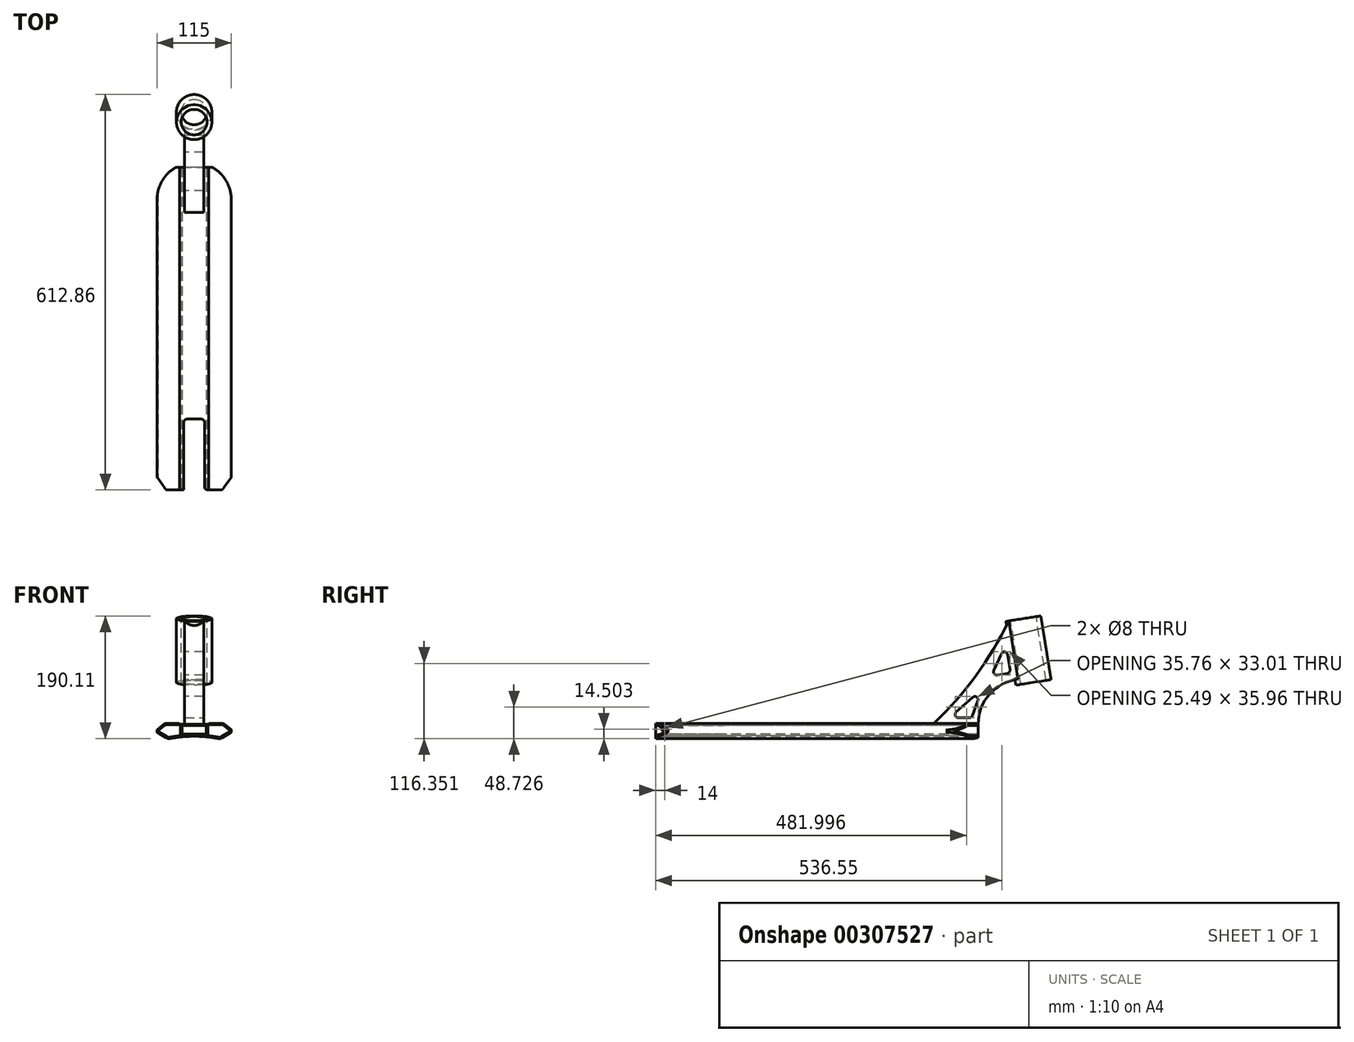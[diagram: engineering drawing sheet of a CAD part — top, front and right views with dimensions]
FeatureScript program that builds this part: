
annotation { "Feature Type Name" : "Feature", "Feature Type Description" : "" }
export const myFeature = defineFeature(function(context is Context, id is Id, definition is map)
    precondition{}
    {
        {
            var Q0;
            Q0=qCreatedBy(makeId("Front.planeOp"),FACE);
            var sketch = newSketch(context, id + "F0", { "sketchPlane" : qUnion([Q0])});
            skLineSegment(sketch, "E0", {"start": v(0, 0) * mm, "end": v(0, 36.76) * mm});
            skLineSegment(sketch, "E1", {"start": v(0, 0) * mm, "end": v(22.5, 0) * mm});
            skLineSegment(sketch, "E2", {"start": v(22.5, 0) * mm, "end": v(22.5, 1.3) * mm});
            skLineSegment(sketch, "E3", {"start": v(22.5, 1.3) * mm, "end": v(45.58, 1.3) * mm});
            skLineSegment(sketch, "E4", {"start": v(45.58, 1.3) * mm, "end": v(57.5, -8.7) * mm});
            skLineSegment(sketch, "E5", {"start": v(57.5, -8.7) * mm, "end": v(57.5, -12.7) * mm});
            skLineSegment(sketch, "E6", {"start": v(57.5, -12.7) * mm, "end": v(40.18, -22.7) * mm});
            skLineSegment(sketch, "E7.MirrorCS", {"start": v(0, 0) * mm, "end": v(-22.5, 0) * mm});
            skLineSegment(sketch, "E8.MirrorCS", {"start": v(-22.5, 1.3) * mm, "end": v(-45.58, 1.3) * mm});
            skLineSegment(sketch, "E9.MirrorCS", {"start": v(-22.5, 0) * mm, "end": v(-22.5, 1.3) * mm});
            skLineSegment(sketch, "E10.MirrorCS", {"start": v(-45.58, 1.3) * mm, "end": v(-57.5, -8.7) * mm});
            skLineSegment(sketch, "E11.MirrorCS", {"start": v(-57.5, -8.7) * mm, "end": v(-57.5, -12.7) * mm});
            skLineSegment(sketch, "E12.MirrorCS", {"start": v(-57.5, -12.7) * mm, "end": v(-40.18, -22.7) * mm});
            skArc(sketch, "E13", {"start": v(40.18, -22.7) * mm, "mid": v(0, -18.62) * mm, "end": v(-40.18, -22.7) * mm});
            skSolve(sketch);
        }
        {
            var Q0;
            Q0 = qSketchRegion(id + "F0", true);
            extrude(context, id + "F1", {"entities" : qUnion([Q0]), "endBound" : BoundingType.SYMMETRIC, "depth" : 500 * mm});
        }
        {
            var Q0;
            Q0=qCreatedBy(makeId("Front.planeOp"),FACE);
            var sketch = newSketch(context, id + "F2", { "sketchPlane" : qUnion([Q0])});
            skLineSegment(sketch, "E14.bottom", {"start": v(-19, -2) * mm, "end": v(19, -2) * mm});
            skLineSegment(sketch, "E14.top", {"start": v(-19, -15) * mm, "end": v(19, -15) * mm});
            skLineSegment(sketch, "E14.left", {"start": v(-19, -2) * mm, "end": v(-19, -15) * mm});
            skLineSegment(sketch, "E14.right", {"start": v(19, -2) * mm, "end": v(19, -15) * mm});
            skSolve(sketch);
        }
        {
            var Q0;
            Q0 = qSketchRegion(id + "F2", true);
            extrude(context, id + "F3", {"entities" : qUnion([Q0]), "operationType" : NewBodyOperationType.REMOVE, "endBound" : BoundingType.SYMMETRIC, "oppositeDirection" : true, "depth" : 500 * mm});
        }
        {
            var Q0;
            Q0=makeQuery(id+"F1.opExtrude","SWEPT_EDGE",EDGE,{"disambiguationData":[OSD([sQuery(id+"F0.wireOp",EDGE,"E2"),sQuery(id+"F0.wireOp",EDGE,"E3")])]});
            var Q1;
            Q1=makeQuery(id+"F1.opExtrude","SWEPT_EDGE",EDGE,{"disambiguationData":[OSD([sQuery(id+"F0.wireOp",EDGE,"E8.MirrorCS"),sQuery(id+"F0.wireOp",EDGE,"E9.MirrorCS")])]});
            fillet(context, id + "F4", {"entities" : qUnion([Q0, Q1]), "radius" : 2 * mm, "tangentPropagation" : true, "allowEdgeOverflow" : false});
        }
        {
            var Q0;
            Q0=makeQuery(id+"F1.opExtrude","SWEPT_EDGE",EDGE,{"disambiguationData":[OSD([sQuery(id+"F0.wireOp",EDGE,"E3"),sQuery(id+"F0.wireOp",EDGE,"E4")])]});
            var Q1;
            Q1=makeQuery(id+"F1.opExtrude","SWEPT_EDGE",EDGE,{"disambiguationData":[OSD([sQuery(id+"F0.wireOp",EDGE,"E8.MirrorCS"),sQuery(id+"F0.wireOp",EDGE,"E10.MirrorCS")])]});
            var Q2;
            Q2=makeQuery(id+"F1.opExtrude","SWEPT_EDGE",EDGE,{"disambiguationData":[OSD([sQuery(id+"F0.wireOp",EDGE,"E6"),sQuery(id+"F0.wireOp",EDGE,"E13")])]});
            var Q3;
            Q3=makeQuery(id+"F1.opExtrude","SWEPT_EDGE",EDGE,{"disambiguationData":[OSD([sQuery(id+"F0.wireOp",EDGE,"E12.MirrorCS"),sQuery(id+"F0.wireOp",EDGE,"E13")])]});
            fillet(context, id + "F5", {"entities" : qUnion([Q0, Q1, Q2, Q3]), "radius" : 9 * mm, "tangentPropagation" : true, "allowEdgeOverflow" : false});
        }
        {
            var Q0;
            Q0=makeQuery(id+"F1.opExtrude","SWEPT_EDGE",EDGE,{"disambiguationData":[OSD([sQuery(id+"F0.wireOp",EDGE,"E4"),sQuery(id+"F0.wireOp",EDGE,"E5")])]});
            var Q1;
            Q1=makeQuery(id+"F1.opExtrude","SWEPT_EDGE",EDGE,{"disambiguationData":[OSD([sQuery(id+"F0.wireOp",EDGE,"E5"),sQuery(id+"F0.wireOp",EDGE,"E6")])]});
            var Q2;
            Q2=makeQuery(id+"F1.opExtrude","SWEPT_EDGE",EDGE,{"disambiguationData":[OSD([sQuery(id+"F0.wireOp",EDGE,"E10.MirrorCS"),sQuery(id+"F0.wireOp",EDGE,"E11.MirrorCS")])]});
            var Q3;
            Q3=makeQuery(id+"F1.opExtrude","SWEPT_EDGE",EDGE,{"disambiguationData":[OSD([sQuery(id+"F0.wireOp",EDGE,"E11.MirrorCS"),sQuery(id+"F0.wireOp",EDGE,"E12.MirrorCS")])]});
            fillet(context, id + "F6", {"entities" : qUnion([Q0, Q1, Q2, Q3]), "radius" : 1 * mm, "tangentPropagation" : true, "allowEdgeOverflow" : false});
        }
        {
            var Q0;
            Q0=makeQuery(id+"F1.opExtrude","CAP_FACE",FACE,{"disambiguationData":[OSD([sQuery(id+"F0.wireOp",EDGE,"E1"),sQuery(id+"F0.wireOp",EDGE,"E2"),sQuery(id+"F0.wireOp",EDGE,"E3"),sQuery(id+"F0.wireOp",EDGE,"E4"),sQuery(id+"F0.wireOp",EDGE,"E5"),sQuery(id+"F0.wireOp",EDGE,"E6"),sQuery(id+"F0.wireOp",EDGE,"E7.MirrorCS"),sQuery(id+"F0.wireOp",EDGE,"E8.MirrorCS"),sQuery(id+"F0.wireOp",EDGE,"E9.MirrorCS"),sQuery(id+"F0.wireOp",EDGE,"E10.MirrorCS"),sQuery(id+"F0.wireOp",EDGE,"E11.MirrorCS"),sQuery(id+"F0.wireOp",EDGE,"E12.MirrorCS"),sQuery(id+"F0.wireOp",EDGE,"E13")])],"isStart":false});
            var sketch = newSketch(context, id + "F7", { "sketchPlane" : qUnion([Q0])});
            skArc(sketch, "E15.0", {"start": v(37.3, -20.1) * mm, "mid": v(0, -16.62) * mm, "end": v(-37.3, -20.1) * mm});
            skArc(sketch, "E15.1", {"start": v(-42.1, -19.28) * mm, "mid": v(-39.78, -20.12) * mm, "end": v(-37.3, -20.1) * mm});
            skLineSegment(sketch, "E15.2", {"start": v(-24.37, -0.7) * mm, "end": v(-42.3, -0.7) * mm});
            skArc(sketch, "E15.3", {"start": v(-42.3, -0.7) * mm, "mid": v(-44.7, -1.12) * mm, "end": v(-46.8, -2.34) * mm});
            skLineSegment(sketch, "E15.4", {"start": v(-46.8, -2.34) * mm, "end": v(-55.76, -9.85) * mm});
            skLineSegment(sketch, "E15.5", {"start": v(-55.61, -11.48) * mm, "end": v(-42.1, -19.28) * mm});
            skPoint(sketch, "E16.visualSharp", {"position": v(-56.85, -10.77) * mm});
            skArc(sketch, "E16.filletArc", {"start": v(-55.76, -9.85) * mm, "mid": v(-56.1, -10.7) * mm, "end": v(-55.61, -11.48) * mm});
            skArc(sketch, "E17", {"start": v(-22.5, -2) * mm, "mid": v(-23.23, -1.06) * mm, "end": v(-24.37, -0.7) * mm});
            skLineSegment(sketch, "E18", {"start": v(-22.5, -2) * mm, "end": v(-21, -2) * mm});
            skLineSegment(sketch, "E19", {"start": v(-21, -2) * mm, "end": v(-21, -17.72) * mm});
            skLineSegment(sketch, "E20.MirrorCS", {"start": v(21, -2) * mm, "end": v(21, -17.72) * mm});
            skLineSegment(sketch, "E21.MirrorCS", {"start": v(22.5, -2) * mm, "end": v(21, -2) * mm});
            skArc(sketch, "E22.MirrorCS", {"start": v(22.5, -2) * mm, "mid": v(23.23, -1.06) * mm, "end": v(24.37, -0.7) * mm});
            skLineSegment(sketch, "E23.MirrorCS", {"start": v(24.37, -0.7) * mm, "end": v(42.3, -0.7) * mm});
            skArc(sketch, "E24.MirrorCS", {"start": v(42.3, -0.7) * mm, "mid": v(44.7, -1.12) * mm, "end": v(46.8, -2.34) * mm});
            skLineSegment(sketch, "E25.MirrorCS", {"start": v(46.8, -2.34) * mm, "end": v(55.76, -9.85) * mm});
            skArc(sketch, "E26.MirrorCS", {"start": v(55.76, -9.85) * mm, "mid": v(56.1, -10.7) * mm, "end": v(55.61, -11.48) * mm});
            skLineSegment(sketch, "E27.MirrorCS", {"start": v(55.61, -11.48) * mm, "end": v(42.1, -19.28) * mm});
            skArc(sketch, "E28.MirrorCS", {"start": v(42.1, -19.28) * mm, "mid": v(39.78, -20.12) * mm, "end": v(37.3, -20.1) * mm});
            skArc(sketch, "E29.MirrorCS", {"start": v(-37.3, -20.1) * mm, "mid": v(0, -16.62) * mm, "end": v(37.3, -20.1) * mm});
            skSolve(sketch);
        }
        {
            var Q0;
            {var subQ0=sQuery(id+"F7.wireOp",EDGE,"E15.1");Q0=makeQuery(id+"F7.imprint","IMPRINT",FACE,{"disambiguationData":[TD([[makeQuery(id+"F7.imprint","IMPRINT",EDGE,{"derivedFrom":subQ0}),1.0]])]});}
            var Q1;
            {var subQ0=sQuery(id+"F7.wireOp",EDGE,"E20.MirrorCS");Q1=makeQuery(id+"F7.imprint","IMPRINT",FACE,{"disambiguationData":[TD([[makeQuery(id+"F7.imprint","IMPRINT",EDGE,{"derivedFrom":subQ0}),1.0]])]});}
            extrude(context, id + "F8", {"entities" : qUnion([Q0, Q1]), "operationType" : NewBodyOperationType.REMOVE, "endBound" : BoundingType.THROUGH_ALL, "oppositeDirection" : true, "depth" : 25 * mm});
        }
        {
            var Q0;
            Q0=qCreatedBy(makeId("Top.planeOp"),FACE);
            var sketch = newSketch(context, id + "F9", { "sketchPlane" : qUnion([Q0])});
            skArc(sketch, "E30", {"start": v(57.5, 200) * mm, "mid": v(0, 257.5) * mm, "end": v(-57.5, 200) * mm});
            skLineSegment(sketch, "E31", {"start": v(-57.5, 200) * mm, "end": v(-57.5, 280) * mm});
            skLineSegment(sketch, "E32", {"start": v(-57.5, 280) * mm, "end": v(57.5, 280) * mm});
            skLineSegment(sketch, "E33", {"start": v(57.5, 280) * mm, "end": v(57.5, 200) * mm});
            skSolve(sketch);
        }
        {
            var Q0;
            Q0=makeQuery(id+"F9.imprint","IMPRINT",FACE,{"disambiguationData":[TD([[makeQuery(id+"F9.imprint","IMPRINT",EDGE,{"derivedFrom":sQuery(id+"F9.wireOp",EDGE,"E30")}),-1.0]])]});
            extrude(context, id + "F10", {"entities" : qUnion([Q0]), "operationType" : NewBodyOperationType.REMOVE, "endBound" : BoundingType.THROUGH_ALL, "depth" : 25 * mm, "hasSecondDirection" : true, "secondDirectionBound" : SecondDirectionBoundingType.THROUGH_ALL, "secondDirectionOppositeDirection" : true, "secondDirectionDepth" : 25 * mm});
        }
        {
            var Q0;
            Q0=qCreatedBy(makeId("Top.planeOp"),FACE);
            var sketch = newSketch(context, id + "F11", { "sketchPlane" : qUnion([Q0])});
            skLineSegment(sketch, "E34", {"start": v(-68, -216) * mm, "end": v(-43.3, -250) * mm});
            skLineSegment(sketch, "E35", {"start": v(-43.3, -250) * mm, "end": v(-16, -250) * mm});
            skLineSegment(sketch, "E36", {"start": v(-16, -250) * mm, "end": v(-16, -140) * mm});
            skLineSegment(sketch, "E37", {"start": v(-16, -140) * mm, "end": v(16, -140) * mm});
            skLineSegment(sketch, "E38", {"start": v(16, -140) * mm, "end": v(16, -250) * mm});
            skLineSegment(sketch, "E39", {"start": v(16, -250) * mm, "end": v(43.3, -250) * mm});
            skLineSegment(sketch, "E40", {"start": v(43.3, -250) * mm, "end": v(68, -216) * mm});
            skLineSegment(sketch, "E41", {"start": v(68, -216) * mm, "end": v(68, -346) * mm});
            skLineSegment(sketch, "E42", {"start": v(68, -346) * mm, "end": v(-68, -346) * mm});
            skLineSegment(sketch, "E43", {"start": v(-68, -346) * mm, "end": v(-68, -216) * mm});
            skSolve(sketch);
        }
        {
            var Q0;
            Q0=makeQuery(id+"F11.imprint","IMPRINT",FACE,{"disambiguationData":[TD([[makeQuery(id+"F11.imprint","IMPRINT",EDGE,{"derivedFrom":sQuery(id+"F11.wireOp",EDGE,"E34")}),-1.0]])]});
            extrude(context, id + "F12", {"entities" : qUnion([Q0]), "operationType" : NewBodyOperationType.REMOVE, "endBound" : BoundingType.THROUGH_ALL, "oppositeDirection" : true, "depth" : 25 * mm, "hasSecondDirection" : true, "secondDirectionBound" : SecondDirectionBoundingType.THROUGH_ALL, "secondDirectionOppositeDirection" : false, "secondDirectionDepth" : 25 * mm});
        }
        {
            var Q0;
            {var subQ2=sQuery(id+"F11.wireOp",EDGE,"E36");Q0=makeQuery(id+"F12.boolean.opBoolean","COPY",EDGE,{"disambiguationData":[TD([makeQuery(id+"F3.boolean.opBoolean","COPY",FACE,{"derivedFrom":makeQuery(id+"F3.opExtrude","SWEPT_FACE",FACE,{"disambiguationData":[OSD([sQuery(id+"F2.wireOp",EDGE,"E14.bottom")])]})})])],"derivedFrom":makeQuery(id+"F12.opExtrude","SWEPT_EDGE",EDGE,{"disambiguationData":[OSD([sQuery(id+"F11.wireOp",EDGE,"E35"),subQ2])]})});}
            var Q1;
            {var subQ0=sQuery(id+"F0.wireOp",EDGE,"E13");var subQ1=sQuery(id+"F11.wireOp",EDGE,"E36");Q1=makeQuery(id+"F12.boolean.opBoolean","COPY",EDGE,{"disambiguationData":[TD([makeQuery(id+"F1.opExtrude","SWEPT_FACE",FACE,{"disambiguationData":[OSD([subQ0])]})])],"derivedFrom":makeQuery(id+"F12.opExtrude","SWEPT_EDGE",EDGE,{"disambiguationData":[OSD([sQuery(id+"F11.wireOp",EDGE,"E35"),subQ1])]})});}
            var Q2;
            {var subQ0=sQuery(id+"F11.wireOp",EDGE,"E36");var subQ1=sQuery(id+"F11.wireOp",EDGE,"E37");Q2=makeQuery(id+"F12.boolean.opBoolean","COPY",EDGE,{"disambiguationData":[TD([makeQuery(id+"F3.boolean.opBoolean","COPY",FACE,{"derivedFrom":makeQuery(id+"F3.opExtrude","SWEPT_FACE",FACE,{"disambiguationData":[OSD([sQuery(id+"F2.wireOp",EDGE,"E14.bottom")])]})})])],"derivedFrom":makeQuery(id+"F12.opExtrude","SWEPT_EDGE",EDGE,{"disambiguationData":[OSD([subQ0,subQ1])]})});}
            var Q3;
            {var subQ0=sQuery(id+"F11.wireOp",EDGE,"E37");var subQ1=sQuery(id+"F11.wireOp",EDGE,"E36");Q3=makeQuery(id+"F12.boolean.opBoolean","COPY",EDGE,{"disambiguationData":[TD([makeQuery(id+"F1.opExtrude","SWEPT_FACE",FACE,{"disambiguationData":[OSD([sQuery(id+"F0.wireOp",EDGE,"E13")])]})])],"derivedFrom":makeQuery(id+"F12.opExtrude","SWEPT_EDGE",EDGE,{"disambiguationData":[OSD([subQ1,subQ0])]})});}
            var Q4;
            {var subQ0=sQuery(id+"F11.wireOp",EDGE,"E38");var subQ1=sQuery(id+"F11.wireOp",EDGE,"E37");Q4=makeQuery(id+"F12.boolean.opBoolean","COPY",EDGE,{"disambiguationData":[TD([makeQuery(id+"F3.boolean.opBoolean","COPY",FACE,{"derivedFrom":makeQuery(id+"F3.opExtrude","SWEPT_FACE",FACE,{"disambiguationData":[OSD([sQuery(id+"F2.wireOp",EDGE,"E14.bottom")])]})})])],"derivedFrom":makeQuery(id+"F12.opExtrude","SWEPT_EDGE",EDGE,{"disambiguationData":[OSD([subQ1,subQ0])]})});}
            var Q5;
            {var subQ0=sQuery(id+"F11.wireOp",EDGE,"E37");var subQ1=sQuery(id+"F11.wireOp",EDGE,"E38");Q5=makeQuery(id+"F12.boolean.opBoolean","COPY",EDGE,{"disambiguationData":[TD([makeQuery(id+"F1.opExtrude","SWEPT_FACE",FACE,{"disambiguationData":[OSD([sQuery(id+"F0.wireOp",EDGE,"E13")])]})])],"derivedFrom":makeQuery(id+"F12.opExtrude","SWEPT_EDGE",EDGE,{"disambiguationData":[OSD([subQ0,subQ1])]})});}
            var Q6;
            {var subQ2=sQuery(id+"F11.wireOp",EDGE,"E38");Q6=makeQuery(id+"F12.boolean.opBoolean","COPY",EDGE,{"disambiguationData":[TD([makeQuery(id+"F3.boolean.opBoolean","COPY",FACE,{"derivedFrom":makeQuery(id+"F3.opExtrude","SWEPT_FACE",FACE,{"disambiguationData":[OSD([sQuery(id+"F2.wireOp",EDGE,"E14.bottom")])]})})])],"derivedFrom":makeQuery(id+"F12.opExtrude","SWEPT_EDGE",EDGE,{"disambiguationData":[OSD([subQ2,sQuery(id+"F11.wireOp",EDGE,"E39")])]})});}
            var Q7;
            {var subQ0=sQuery(id+"F0.wireOp",EDGE,"E13");var subQ1=sQuery(id+"F11.wireOp",EDGE,"E38");Q7=makeQuery(id+"F12.boolean.opBoolean","COPY",EDGE,{"disambiguationData":[TD([makeQuery(id+"F1.opExtrude","SWEPT_FACE",FACE,{"disambiguationData":[OSD([subQ0])]})])],"derivedFrom":makeQuery(id+"F12.opExtrude","SWEPT_EDGE",EDGE,{"disambiguationData":[OSD([subQ1,sQuery(id+"F11.wireOp",EDGE,"E39")])]})});}
            fillet(context, id + "F13", {"entities" : qUnion([Q0, Q1, Q2, Q3, Q4, Q5, Q6, Q7]), "radius" : 5 * mm, "tangentPropagation" : true, "allowEdgeOverflow" : false});
        }
        {
            var Q0;
            Q0=qCreatedBy(makeId("Right.planeOp"),FACE);
            var sketch = newSketch(context, id + "F14", { "sketchPlane" : qUnion([Q0])});
            skLineSegment(sketch, "E44", {"start": v(250, 0) * mm, "end": v(180, 0) * mm});
            skArc(sketch, "E45", {"start": v(311.71, 69.5) * mm, "mid": v(267.66, 46.48) * mm, "end": v(250, 0) * mm});
            skArc(sketch, "E46", {"start": v(180, 0) * mm, "mid": v(245.97, 74.66) * mm, "end": v(297.38, 160) * mm});
            skLineSegment(sketch, "E47", {"start": v(297.38, 160) * mm, "end": v(342.82, 167.2) * mm});
            skLineSegment(sketch, "E48", {"start": v(342.82, 167.2) * mm, "end": v(358.46, 68.43) * mm});
            skLineSegment(sketch, "E49", {"start": v(358.46, 68.43) * mm, "end": v(313.03, 61.23) * mm});
            skLineSegment(sketch, "E50", {"start": v(311.71, 69.5) * mm, "end": v(313.03, 61.23) * mm});
            skSolve(sketch);
        }
        {
            var Q0;
            Q0 = qSketchRegion(id + "F14", true);
            extrude(context, id + "F15", {"entities" : qUnion([Q0]), "operationType" : NewBodyOperationType.ADD, "endBound" : BoundingType.SYMMETRIC, "depth" : 30 * mm});
        }
        {
            var Q0;
            Q0=makeQuery(id+"F15.opExtrude","SWEPT_FACE",FACE,{"disambiguationData":[OSD([sQuery(id+"F14.wireOp",EDGE,"E47")])]});
            var sketch = newSketch(context, id + "F16", { "sketchPlane" : qUnion([Q0])});
            skCircle(sketch, "E51", {"center": v(0, 341.75) * mm, "radius": 27.46 * mm});
            skSolve(sketch);
        }
        {
            var Q0;
            Q0 = qSketchRegion(id + "F16", true);
            var Q1;
            Q1=makeQuery(id+"F15.opExtrude","SWEPT_FACE",FACE,{"disambiguationData":[OSD([sQuery(id+"F14.wireOp",EDGE,"E49")])]});
            extrude(context, id + "F17", {"entities" : qUnion([Q0]), "operationType" : NewBodyOperationType.ADD, "endBound" : BoundingType.UP_TO_SURFACE, "oppositeDirection" : true, "endBoundEntityFace" : qUnion([Q1]), "depth" : 25 * mm});
        }
        {
            var Q0;
            Q0=makeQuery(id+"F17.boolean.opBoolean","MERGE",FACE,{"derivedFrom":[makeQuery(id+"F15.opExtrude","SWEPT_FACE",FACE,{"disambiguationData":[OSD([sQuery(id+"F14.wireOp",EDGE,"E47")])]}),makeQuery(id+"F17.opExtrude","CAP_FACE",FACE,{"disambiguationData":[OSD([sQuery(id+"F16.wireOp",EDGE,"E51")])],"isStart":true})]});
            var sketch = newSketch(context, id + "F18", { "sketchPlane" : qUnion([Q0])});
            skPoint(sketch, "E52", {"position": v(0, 341.75) * mm});
            skSolve(sketch);
        }
        {
            var Q0;
            Q0=sQuery(id+"F18.wireOp",VERTEX,"E52");
            var Q1;
            Q1=makeQuery(id+"F1.opExtrude","SWEPT_BODY",BODY,{"disambiguationData":[OSD([sQuery(id+"F0.wireOp",EDGE,"E1"),sQuery(id+"F0.wireOp",EDGE,"E2"),sQuery(id+"F0.wireOp",EDGE,"E3"),sQuery(id+"F0.wireOp",EDGE,"E4"),sQuery(id+"F0.wireOp",EDGE,"E5"),sQuery(id+"F0.wireOp",EDGE,"E6"),sQuery(id+"F0.wireOp",EDGE,"E7.MirrorCS"),sQuery(id+"F0.wireOp",EDGE,"E8.MirrorCS"),sQuery(id+"F0.wireOp",EDGE,"E9.MirrorCS"),sQuery(id+"F0.wireOp",EDGE,"E10.MirrorCS"),sQuery(id+"F0.wireOp",EDGE,"E11.MirrorCS"),sQuery(id+"F0.wireOp",EDGE,"E12.MirrorCS"),sQuery(id+"F0.wireOp",EDGE,"E13")])]});
            hole(context, id + "F19", {"style" : HoleStyle.SIMPLE, "endStyle" : HoleEndStyle.THROUGH, "holeDiameter" : 40 * mm, "isTappedThrough" : true, "tappedDepth" : 12 * mm, "tapClearance" : 3, "locations" : qUnion([Q0]), "scope" : qUnion([Q1])});
        }
        {
            var Q0;
            Q0=makeQuery(id+"F8.boolean.opBoolean","COPY",FACE,{"derivedFrom":makeQuery(id+"F8.opExtrude","SWEPT_FACE",FACE,{"disambiguationData":[OSD([sQuery(id+"F7.wireOp",EDGE,"E20.MirrorCS")])]})});
            var sketch = newSketch(context, id + "F20", { "sketchPlane" : qUnion([Q0])});
            skPoint(sketch, "E53", {"position": v(-236, -7.72) * mm});
            skSolve(sketch);
        }
        {
            var Q0;
            Q0=sQuery(id+"F20.wireOp",VERTEX,"E53");
            var Q1;
            Q1=makeQuery(id+"F1.opExtrude","SWEPT_BODY",BODY,{"disambiguationData":[OSD([sQuery(id+"F0.wireOp",EDGE,"E1"),sQuery(id+"F0.wireOp",EDGE,"E2"),sQuery(id+"F0.wireOp",EDGE,"E3"),sQuery(id+"F0.wireOp",EDGE,"E4"),sQuery(id+"F0.wireOp",EDGE,"E5"),sQuery(id+"F0.wireOp",EDGE,"E6"),sQuery(id+"F0.wireOp",EDGE,"E7.MirrorCS"),sQuery(id+"F0.wireOp",EDGE,"E8.MirrorCS"),sQuery(id+"F0.wireOp",EDGE,"E9.MirrorCS"),sQuery(id+"F0.wireOp",EDGE,"E10.MirrorCS"),sQuery(id+"F0.wireOp",EDGE,"E11.MirrorCS"),sQuery(id+"F0.wireOp",EDGE,"E12.MirrorCS"),sQuery(id+"F0.wireOp",EDGE,"E13")])]});
            hole(context, id + "F21", {"style" : HoleStyle.SIMPLE, "endStyle" : HoleEndStyle.BLIND, "holeDiameter" : 8 * mm, "holeDepth" : 50 * mm, "isTappedThrough" : true, "tappedDepth" : 12 * mm, "tapClearance" : 3, "locations" : qUnion([Q0]), "scope" : qUnion([Q1])});
        }
        {
            var Q0;
            Q0=makeQuery(id+"F15.opExtrude","CAP_FACE",FACE,{"disambiguationData":[OSD([sQuery(id+"F14.wireOp",EDGE,"E44"),sQuery(id+"F14.wireOp",EDGE,"E45"),sQuery(id+"F14.wireOp",EDGE,"E46"),sQuery(id+"F14.wireOp",EDGE,"E47"),sQuery(id+"F14.wireOp",EDGE,"E48"),sQuery(id+"F14.wireOp",EDGE,"E49"),sQuery(id+"F14.wireOp",EDGE,"E50")])],"isStart":false});
            var sketch = newSketch(context, id + "F22", { "sketchPlane" : qUnion([Q0])});
            skLineSegment(sketch, "E54", {"start": v(206, 10) * mm, "end": v(240, 10) * mm});
            skLineSegment(sketch, "E55", {"start": v(240, 10) * mm, "end": v(256.38, 55) * mm});
            skLineSegment(sketch, "E56", {"start": v(256.38, 55) * mm, "end": v(206, 10) * mm});
            skLineSegment(sketch, "E57", {"start": v(270.39, 74.73) * mm, "end": v(300.02, 79.42) * mm});
            skLineSegment(sketch, "E58", {"start": v(300.02, 79.42) * mm, "end": v(292.9, 124.42) * mm});
            skLineSegment(sketch, "E59", {"start": v(292.9, 124.42) * mm, "end": v(270.39, 74.73) * mm});
            skSolve(sketch);
        }
        {
            var Q0;
            Q0 = qSketchRegion(id + "F22", true);
            extrude(context, id + "F23", {"entities" : qUnion([Q0]), "operationType" : NewBodyOperationType.REMOVE, "endBound" : BoundingType.THROUGH_ALL, "oppositeDirection" : true, "depth" : 25 * mm});
        }
        {
            var Q0;
            Q0=makeQuery(id+"F23.boolean.opBoolean","COPY",EDGE,{"derivedFrom":makeQuery(id+"F23.opExtrude","SWEPT_EDGE",EDGE,{"disambiguationData":[OSD([sQuery(id+"F22.wireOp",EDGE,"E58"),sQuery(id+"F22.wireOp",EDGE,"E59")])]})});
            var Q1;
            Q1=makeQuery(id+"F23.boolean.opBoolean","COPY",EDGE,{"derivedFrom":makeQuery(id+"F23.opExtrude","SWEPT_EDGE",EDGE,{"disambiguationData":[OSD([sQuery(id+"F22.wireOp",EDGE,"E57"),sQuery(id+"F22.wireOp",EDGE,"E59")])]})});
            var Q2;
            Q2=makeQuery(id+"F23.boolean.opBoolean","COPY",EDGE,{"derivedFrom":makeQuery(id+"F23.opExtrude","SWEPT_EDGE",EDGE,{"disambiguationData":[OSD([sQuery(id+"F22.wireOp",EDGE,"E57"),sQuery(id+"F22.wireOp",EDGE,"E58")])]})});
            var Q3;
            Q3=makeQuery(id+"F23.boolean.opBoolean","COPY",EDGE,{"derivedFrom":makeQuery(id+"F23.opExtrude","SWEPT_EDGE",EDGE,{"disambiguationData":[OSD([sQuery(id+"F22.wireOp",EDGE,"E54"),sQuery(id+"F22.wireOp",EDGE,"E55")])]})});
            var Q4;
            Q4=makeQuery(id+"F23.boolean.opBoolean","COPY",EDGE,{"derivedFrom":makeQuery(id+"F23.opExtrude","SWEPT_EDGE",EDGE,{"disambiguationData":[OSD([sQuery(id+"F22.wireOp",EDGE,"E54"),sQuery(id+"F22.wireOp",EDGE,"E56")])]})});
            var Q5;
            Q5=makeQuery(id+"F23.boolean.opBoolean","COPY",EDGE,{"derivedFrom":makeQuery(id+"F23.opExtrude","SWEPT_EDGE",EDGE,{"disambiguationData":[OSD([sQuery(id+"F22.wireOp",EDGE,"E55"),sQuery(id+"F22.wireOp",EDGE,"E56")])]})});
            fillet(context, id + "F24", {"entities" : qUnion([Q0, Q1, Q2, Q3, Q4, Q5]), "radius" : 5 * mm, "tangentPropagation" : true, "allowEdgeOverflow" : false});
        }
    });
